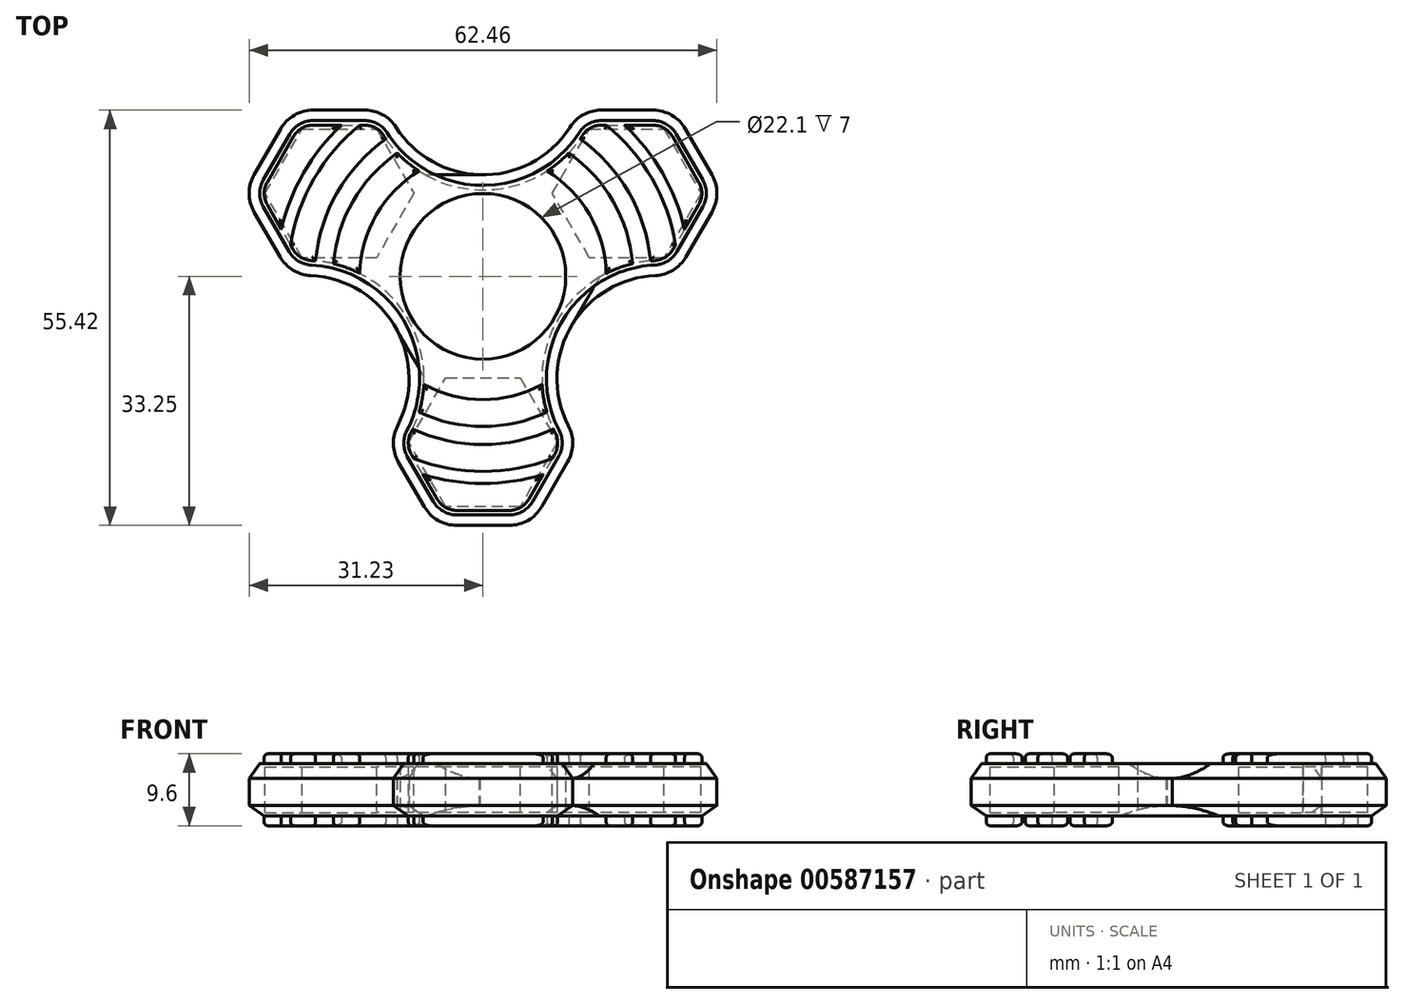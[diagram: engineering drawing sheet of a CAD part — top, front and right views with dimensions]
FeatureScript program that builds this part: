
annotation { "Feature Type Name" : "Feature", "Feature Type Description" : "" }
export const myFeature = defineFeature(function(context is Context, id is Id, definition is map)
    precondition{}
    {
        {
            var Q0;
            Q0=qCreatedBy(makeId("Top.planeOp"),FACE);
            var sketch = newSketch(context, id + "F0", { "sketchPlane" : qUnion([Q0])});
            skCircle(sketch, "E0", {"center": v(0, 0) * mm, "radius": 11.05 * mm});
            skCircle(sketch, "E1.cCircle", {"center": v(0, -22.15) * mm, "radius": 8.6 * mm, "construction": true});
            skLineSegment(sketch, "E1.0", {"start": v(4.97, -30.75) * mm, "end": v(-4.97, -30.75) * mm});
            skLineSegment(sketch, "E1.1", {"start": v(-4.97, -30.75) * mm, "end": v(-9.93, -22.15) * mm});
            skLineSegment(sketch, "E1.2", {"start": v(-9.93, -22.15) * mm, "end": v(-4.97, -13.55) * mm});
            skLineSegment(sketch, "E1.3", {"start": v(-4.97, -13.55) * mm, "end": v(4.97, -13.55) * mm});
            skLineSegment(sketch, "E1.4", {"start": v(4.97, -13.55) * mm, "end": v(9.93, -22.15) * mm});
            skLineSegment(sketch, "E1.5", {"start": v(9.93, -22.15) * mm, "end": v(4.97, -30.75) * mm});
            skPoint(sketch, "E1.0.midPoint", {"position": v(0, -30.75) * mm});
            skCircle(sketch, "E2.0", {"center": v(0, 0) * mm, "radius": 13.55 * mm});
            skLineSegment(sketch, "E3.3", {"start": v(3.52, -33.25) * mm, "end": v(-3.52, -33.25) * mm});
            skLineSegment(sketch, "E3.4", {"start": v(-7.85, -30.75) * mm, "end": v(-11.3, -24.77) * mm});
            skPoint(sketch, "E4.visualSharp", {"position": v(-6.4, -33.25) * mm});
            skArc(sketch, "E4.filletArc", {"start": v(-7.85, -30.75) * mm, "mid": v(-6.02, -32.58) * mm, "end": v(-3.52, -33.25) * mm});
            skPoint(sketch, "E5.visualSharp", {"position": v(6.4, -33.25) * mm});
            skArc(sketch, "E5.filletArc", {"start": v(3.52, -33.25) * mm, "mid": v(6.02, -32.58) * mm, "end": v(7.85, -30.75) * mm});
            skPoint(sketch, "E6.third.point", {"position": v(-11.94, -6.4) * mm});
            skPoint(sketch, "E7.third.point", {"position": v(11.98, -6.33) * mm});
            skLineSegment(sketch, "E8", {"start": v(11.3, -24.77) * mm, "end": v(7.85, -30.75) * mm});
            skArc(sketch, "E9", {"start": v(-11.42, -19.97) * mm, "mid": v(-9.89, -13.12) * mm, "end": v(-11.94, -6.4) * mm});
            skArc(sketch, "E10", {"start": v(11.98, -6.33) * mm, "mid": v(9.89, -13.08) * mm, "end": v(11.41, -19.97) * mm});
            skPoint(sketch, "E11.visualSharp", {"position": v(-12.82, -22.15) * mm});
            skArc(sketch, "E11.filletArc", {"start": v(-11.42, -19.97) * mm, "mid": v(-11.97, -22.38) * mm, "end": v(-11.3, -24.77) * mm});
            skPoint(sketch, "E12.visualSharp", {"position": v(12.82, -22.15) * mm});
            skArc(sketch, "E12.filletArc", {"start": v(11.3, -24.77) * mm, "mid": v(11.97, -22.38) * mm, "end": v(11.41, -19.97) * mm});
            skPoint(sketch, "E13.1.0", {"position": v(25.6, 22.17) * mm});
            skLineSegment(sketch, "E13.1.1", {"start": v(9.25, 11.07) * mm, "end": v(14.22, 19.68) * mm});
            skPoint(sketch, "E13.1.2", {"position": v(26.63, 15.37) * mm});
            skCircle(sketch, "E13.1.3", {"center": v(19.18, 11.07) * mm, "radius": 8.6 * mm, "construction": true});
            skLineSegment(sketch, "E13.1.4", {"start": v(29.11, 11.07) * mm, "end": v(24.15, 2.47) * mm});
            skLineSegment(sketch, "E13.1.5", {"start": v(15.8, 22.17) * mm, "end": v(22.7, 22.17) * mm});
            skPoint(sketch, "E13.1.6", {"position": v(32, 11.07) * mm});
            skPoint(sketch, "E13.1.7", {"position": v(25.6, -0.02) * mm});
            skLineSegment(sketch, "E13.1.8", {"start": v(27.03, 19.67) * mm, "end": v(30.56, 13.57) * mm});
            skLineSegment(sketch, "E13.1.9", {"start": v(24.15, 2.47) * mm, "end": v(14.22, 2.47) * mm});
            skLineSegment(sketch, "E13.1.10", {"start": v(14.22, 2.48) * mm, "end": v(9.25, 11.07) * mm});
            skLineSegment(sketch, "E13.1.11", {"start": v(24.15, 19.67) * mm, "end": v(29.11, 11.07) * mm});
            skLineSegment(sketch, "E13.1.12", {"start": v(14.22, 19.68) * mm, "end": v(24.15, 19.67) * mm});
            skPoint(sketch, "E13.1.13", {"position": v(12.77, 22.17) * mm});
            skLineSegment(sketch, "E13.1.14", {"start": v(30.56, 8.57) * mm, "end": v(27.1, 2.6) * mm});
            skArc(sketch, "E13.1.15", {"start": v(27.03, 19.67) * mm, "mid": v(25.2, 21.5) * mm, "end": v(22.7, 22.17) * mm});
            skArc(sketch, "E13.1.16", {"start": v(15.8, 22.17) * mm, "mid": v(13.4, 21.56) * mm, "end": v(11.59, 19.87) * mm});
            skArc(sketch, "E13.1.17", {"start": v(30.56, 8.57) * mm, "mid": v(31.23, 11.07) * mm, "end": v(30.56, 13.57) * mm});
            skArc(sketch, "E13.1.18", {"start": v(23, 0.1) * mm, "mid": v(25.37, 0.82) * mm, "end": v(27.1, 2.6) * mm});
            skArc(sketch, "E13.1.19", {"start": v(-0.5, 13.54) * mm, "mid": v(6.38, 15.1) * mm, "end": v(11.59, 19.87) * mm});
            skArc(sketch, "E13.1.20", {"start": v(23, 0.1) * mm, "mid": v(16.3, -2) * mm, "end": v(11.52, -7.14) * mm});
            skPoint(sketch, "E13.2.0", {"position": v(-32, 11.08) * mm});
            skLineSegment(sketch, "E13.2.1", {"start": v(-14.22, 2.48) * mm, "end": v(-24.15, 2.48) * mm});
            skPoint(sketch, "E13.2.2", {"position": v(-26.63, 15.38) * mm});
            skCircle(sketch, "E13.2.3", {"center": v(-19.18, 11.08) * mm, "radius": 8.6 * mm, "construction": true});
            skLineSegment(sketch, "E13.2.4", {"start": v(-24.15, 19.68) * mm, "end": v(-14.22, 19.68) * mm});
            skLineSegment(sketch, "E13.2.5", {"start": v(-27.1, 2.6) * mm, "end": v(-30.56, 8.58) * mm});
            skPoint(sketch, "E13.2.6", {"position": v(-25.6, 22.17) * mm});
            skPoint(sketch, "E13.2.7", {"position": v(-12.77, 22.17) * mm});
            skLineSegment(sketch, "E13.2.8", {"start": v(-30.56, 13.58) * mm, "end": v(-27.03, 19.67) * mm});
            skLineSegment(sketch, "E13.2.9", {"start": v(-14.22, 19.68) * mm, "end": v(-9.25, 11.08) * mm});
            skLineSegment(sketch, "E13.2.10", {"start": v(-9.25, 11.08) * mm, "end": v(-14.22, 2.48) * mm});
            skLineSegment(sketch, "E13.2.11", {"start": v(-29.11, 11.08) * mm, "end": v(-24.15, 19.68) * mm});
            skLineSegment(sketch, "E13.2.12", {"start": v(-24.15, 2.48) * mm, "end": v(-29.11, 11.08) * mm});
            skPoint(sketch, "E13.2.13", {"position": v(-25.6, -0.02) * mm});
            skLineSegment(sketch, "E13.2.14", {"start": v(-22.7, 22.17) * mm, "end": v(-15.8, 22.17) * mm});
            skArc(sketch, "E13.2.15", {"start": v(-30.56, 13.58) * mm, "mid": v(-31.23, 11.08) * mm, "end": v(-30.56, 8.58) * mm});
            skArc(sketch, "E13.2.16", {"start": v(-27.1, 2.6) * mm, "mid": v(-25.37, 0.82) * mm, "end": v(-23, 0.1) * mm});
            skArc(sketch, "E13.2.17", {"start": v(-22.7, 22.17) * mm, "mid": v(-25.2, 21.5) * mm, "end": v(-27.03, 19.67) * mm});
            skArc(sketch, "E13.2.18", {"start": v(-11.59, 19.87) * mm, "mid": v(-13.4, 21.56) * mm, "end": v(-15.8, 22.17) * mm});
            skArc(sketch, "E13.2.19", {"start": v(-11.47, -7.21) * mm, "mid": v(-16.27, -2.02) * mm, "end": v(-23, 0.1) * mm});
            skArc(sketch, "E13.2.20", {"start": v(-11.59, 19.87) * mm, "mid": v(-6.42, 15.13) * mm, "end": v(0.42, 13.54) * mm});
            skSolve(sketch);
        }
        {
            var Q0;
            Q0=qCreatedBy(makeId("Top.planeOp"),FACE);
            var sketch = newSketch(context, id + "F1", { "sketchPlane" : qUnion([Q0])});
            skArc(sketch, "E14.0", {"start": v(-9.64, -20.9) * mm, "mid": v(-7.9, -13.04) * mm, "end": v(-10.24, -5.36) * mm});
            skArc(sketch, "E14.1", {"start": v(-9.64, -20.9) * mm, "mid": v(-9.97, -22.34) * mm, "end": v(-9.57, -23.77) * mm});
            skLineSegment(sketch, "E14.2", {"start": v(-6.12, -29.75) * mm, "end": v(-9.57, -23.77) * mm});
            skArc(sketch, "E14.3", {"start": v(-6.12, -29.75) * mm, "mid": v(-5.02, -30.85) * mm, "end": v(-3.52, -31.25) * mm});
            skLineSegment(sketch, "E14.4", {"start": v(3.52, -31.25) * mm, "end": v(-3.52, -31.25) * mm});
            skArc(sketch, "E14.5", {"start": v(10.29, -5.27) * mm, "mid": v(7.89, -13) * mm, "end": v(9.64, -20.9) * mm});
            skArc(sketch, "E14.6", {"start": v(9.57, -23.77) * mm, "mid": v(9.97, -22.34) * mm, "end": v(9.64, -20.9) * mm});
            skLineSegment(sketch, "E14.7", {"start": v(9.57, -23.77) * mm, "end": v(6.12, -29.75) * mm});
            skArc(sketch, "E14.8", {"start": v(3.52, -31.25) * mm, "mid": v(5.02, -30.85) * mm, "end": v(6.12, -29.75) * mm});
            skLineSegment(sketch, "E15.1.0", {"start": v(28.82, 9.57) * mm, "end": v(25.37, 3.6) * mm});
            skArc(sketch, "E15.1.1", {"start": v(-0.58, 11.54) * mm, "mid": v(7.3, 13.33) * mm, "end": v(13.27, 18.8) * mm});
            skLineSegment(sketch, "E15.1.2", {"start": v(25.3, 18.67) * mm, "end": v(28.82, 12.58) * mm});
            skLineSegment(sketch, "E15.1.3", {"start": v(15.8, 20.17) * mm, "end": v(22.7, 20.17) * mm});
            skArc(sketch, "E15.1.4", {"start": v(22.91, 2.1) * mm, "mid": v(15.24, -0.31) * mm, "end": v(9.76, -6.19) * mm});
            skArc(sketch, "E15.1.5", {"start": v(22.91, 2.1) * mm, "mid": v(24.33, 2.53) * mm, "end": v(25.37, 3.6) * mm});
            skArc(sketch, "E15.1.6", {"start": v(28.82, 9.57) * mm, "mid": v(29.23, 11.07) * mm, "end": v(28.82, 12.58) * mm});
            skArc(sketch, "E15.1.7", {"start": v(15.8, 20.17) * mm, "mid": v(14.36, 19.8) * mm, "end": v(13.27, 18.8) * mm});
            skArc(sketch, "E15.1.8", {"start": v(25.3, 18.67) * mm, "mid": v(24.2, 19.77) * mm, "end": v(22.7, 20.17) * mm});
            skLineSegment(sketch, "E15.2.0", {"start": v(-22.7, 20.17) * mm, "end": v(-15.8, 20.17) * mm});
            skArc(sketch, "E15.2.1", {"start": v(-9.7, -6.27) * mm, "mid": v(-15.2, -0.33) * mm, "end": v(-22.91, 2.1) * mm});
            skLineSegment(sketch, "E15.2.2", {"start": v(-28.82, 12.58) * mm, "end": v(-25.3, 18.67) * mm});
            skLineSegment(sketch, "E15.2.3", {"start": v(-25.37, 3.6) * mm, "end": v(-28.82, 9.58) * mm});
            skArc(sketch, "E15.2.4", {"start": v(-13.27, 18.8) * mm, "mid": v(-7.35, 13.36) * mm, "end": v(0.48, 11.54) * mm});
            skArc(sketch, "E15.2.5", {"start": v(-13.27, 18.8) * mm, "mid": v(-14.36, 19.8) * mm, "end": v(-15.8, 20.17) * mm});
            skArc(sketch, "E15.2.6", {"start": v(-22.7, 20.17) * mm, "mid": v(-24.2, 19.77) * mm, "end": v(-25.3, 18.67) * mm});
            skArc(sketch, "E15.2.7", {"start": v(-25.37, 3.6) * mm, "mid": v(-24.33, 2.53) * mm, "end": v(-22.91, 2.1) * mm});
            skArc(sketch, "E15.2.8", {"start": v(-28.82, 12.58) * mm, "mid": v(-29.23, 11.08) * mm, "end": v(-28.82, 9.58) * mm});
            skPoint(sketch, "E15.center", {"position": v(0, 0) * mm});
            skCircle(sketch, "E16", {"center": v(0, 0) * mm, "radius": 27.65 * mm});
            skCircle(sketch, "E17", {"center": v(0, 0) * mm, "radius": 26.05 * mm});
            skCircle(sketch, "E18", {"center": v(0, 0) * mm, "radius": 22.45 * mm});
            skCircle(sketch, "E19", {"center": v(0, 0) * mm, "radius": 20.05 * mm});
            skCircle(sketch, "E20", {"center": v(0, 0) * mm, "radius": 16.45 * mm});
            skSolve(sketch);
        }
        {
            var Q0;
            {var subQ1=sQuery(id+"F0.wireOp",EDGE,"E13.2.1");Q0=makeQuery(id+"F0.imprint","IMPRINT",FACE,{"disambiguationData":[TD([[makeQuery(id+"F0.imprint","IMPRINT",EDGE,{"derivedFrom":subQ1}),1.0]])]});}
            var Q1;
            {var subQ1=sQuery(id+"F0.wireOp",EDGE,"E13.1.1");Q1=makeQuery(id+"F0.imprint","IMPRINT",FACE,{"disambiguationData":[TD([[makeQuery(id+"F0.imprint","IMPRINT",EDGE,{"derivedFrom":subQ1}),1.0]])]});}
            var Q2;
            Q2=makeQuery(id+"F0.imprint","IMPRINT",FACE,{"disambiguationData":[TD([[makeQuery(id+"F0.imprint","IMPRINT",EDGE,{"derivedFrom":sQuery(id+"F0.wireOp",EDGE,"E0")}),-1.0]])]});
            var Q3;
            Q3=makeQuery(id+"F0.imprint","IMPRINT",FACE,{"disambiguationData":[TD([[makeQuery(id+"F0.imprint","IMPRINT",EDGE,{"derivedFrom":sQuery(id+"F0.wireOp",EDGE,"E1.0")}),1.0]])]});
            var Q4;
            {var subQ3=sQuery(id+"F0.wireOp",EDGE,"E13.2.1");Q4=makeQuery(id+"F0.imprint","IMPRINT",FACE,{"disambiguationData":[TD([[makeQuery(id+"F0.imprint","IMPRINT",EDGE,{"derivedFrom":subQ3}),-1.0]])]});}
            var Q5;
            {var subQ3=sQuery(id+"F0.wireOp",EDGE,"E13.1.1");Q5=makeQuery(id+"F0.imprint","IMPRINT",FACE,{"disambiguationData":[TD([[makeQuery(id+"F0.imprint","IMPRINT",EDGE,{"derivedFrom":subQ3}),-1.0]])]});}
            var Q6;
            Q6=makeQuery(id+"F0.imprint","IMPRINT",FACE,{"disambiguationData":[TD([[makeQuery(id+"F0.imprint","IMPRINT",EDGE,{"derivedFrom":sQuery(id+"F0.wireOp",EDGE,"E1.0")}),-1.0]])]});
            var Q7;
            Q7=makeQuery(id+"F0.imprint","IMPRINT",FACE,{"disambiguationData":[TD([[makeQuery(id+"F0.imprint","IMPRINT",EDGE,{"derivedFrom":sQuery(id+"F0.wireOp",EDGE,"E0")}),1.0]])]});
            extrude(context, id + "F2", {"entities" : qUnion([Q0, Q1, Q2, Q3, Q4, Q5, Q6, Q7]), "endBound" : BoundingType.SYMMETRIC, "depth" : 7 * mm, "offsetDistance" : 25 * mm});
        }
        {
            var Q0;
            Q0=makeQuery(id+"F2.opExtrude","CAP_FACE",FACE,{"disambiguationData":[OSD([sQuery(id+"F0.wireOp",EDGE,"E0"),sQuery(id+"F0.wireOp",EDGE,"E2.0"),sQuery(id+"F0.wireOp",EDGE,"E3.3"),sQuery(id+"F0.wireOp",EDGE,"E3.4"),sQuery(id+"F0.wireOp",EDGE,"E4.filletArc"),sQuery(id+"F0.wireOp",EDGE,"E5.filletArc"),sQuery(id+"F0.wireOp",EDGE,"E8"),sQuery(id+"F0.wireOp",EDGE,"E9"),sQuery(id+"F0.wireOp",EDGE,"E10"),sQuery(id+"F0.wireOp",EDGE,"E11.filletArc"),sQuery(id+"F0.wireOp",EDGE,"E12.filletArc"),sQuery(id+"F0.wireOp",EDGE,"E13.1.5"),sQuery(id+"F0.wireOp",EDGE,"E13.1.8"),sQuery(id+"F0.wireOp",EDGE,"E13.1.14"),sQuery(id+"F0.wireOp",EDGE,"E13.1.15"),sQuery(id+"F0.wireOp",EDGE,"E13.1.16"),sQuery(id+"F0.wireOp",EDGE,"E13.1.17"),sQuery(id+"F0.wireOp",EDGE,"E13.1.18"),sQuery(id+"F0.wireOp",EDGE,"E13.1.19"),sQuery(id+"F0.wireOp",EDGE,"E13.1.20"),sQuery(id+"F0.wireOp",EDGE,"E13.2.5"),sQuery(id+"F0.wireOp",EDGE,"E13.2.8"),sQuery(id+"F0.wireOp",EDGE,"E13.2.14"),sQuery(id+"F0.wireOp",EDGE,"E13.2.15"),sQuery(id+"F0.wireOp",EDGE,"E13.2.16"),sQuery(id+"F0.wireOp",EDGE,"E13.2.17"),sQuery(id+"F0.wireOp",EDGE,"E13.2.18"),sQuery(id+"F0.wireOp",EDGE,"E13.2.19"),sQuery(id+"F0.wireOp",EDGE,"E13.2.20")])],"isStart":false});
            chamfer(context, id + "F3", {"entities" : qUnion([Q0]), "chamferType" : ChamferType.OFFSET_ANGLE, "width" : 2 * mm, "oppositeDirection" : false, "angle" : 35 * degree, "tangentPropagation" : true});
        }
        {
            var Q0;
            Q0=makeQuery(id+"F2.opExtrude","CAP_FACE",FACE,{"disambiguationData":[OSD([sQuery(id+"F0.wireOp",EDGE,"E2.0"),sQuery(id+"F0.wireOp",EDGE,"E3.3"),sQuery(id+"F0.wireOp",EDGE,"E3.4"),sQuery(id+"F0.wireOp",EDGE,"E4.filletArc"),sQuery(id+"F0.wireOp",EDGE,"E5.filletArc"),sQuery(id+"F0.wireOp",EDGE,"E8"),sQuery(id+"F0.wireOp",EDGE,"E9"),sQuery(id+"F0.wireOp",EDGE,"E10"),sQuery(id+"F0.wireOp",EDGE,"E11.filletArc"),sQuery(id+"F0.wireOp",EDGE,"E12.filletArc"),sQuery(id+"F0.wireOp",EDGE,"E13.1.5"),sQuery(id+"F0.wireOp",EDGE,"E13.1.8"),sQuery(id+"F0.wireOp",EDGE,"E13.1.14"),sQuery(id+"F0.wireOp",EDGE,"E13.1.15"),sQuery(id+"F0.wireOp",EDGE,"E13.1.16"),sQuery(id+"F0.wireOp",EDGE,"E13.1.17"),sQuery(id+"F0.wireOp",EDGE,"E13.1.18"),sQuery(id+"F0.wireOp",EDGE,"E13.1.19"),sQuery(id+"F0.wireOp",EDGE,"E13.1.20"),sQuery(id+"F0.wireOp",EDGE,"E13.2.5"),sQuery(id+"F0.wireOp",EDGE,"E13.2.8"),sQuery(id+"F0.wireOp",EDGE,"E13.2.14"),sQuery(id+"F0.wireOp",EDGE,"E13.2.15"),sQuery(id+"F0.wireOp",EDGE,"E13.2.16"),sQuery(id+"F0.wireOp",EDGE,"E13.2.17"),sQuery(id+"F0.wireOp",EDGE,"E13.2.18"),sQuery(id+"F0.wireOp",EDGE,"E13.2.19"),sQuery(id+"F0.wireOp",EDGE,"E13.2.20")])],"isStart":true});
            chamfer(context, id + "F4", {"entities" : qUnion([Q0]), "chamferType" : ChamferType.OFFSET_ANGLE, "width" : 2 * mm, "oppositeDirection" : false, "angle" : 35 * degree, "tangentPropagation" : true});
        }
        {
            var Q0;
            Q0=makeQuery(id+"F1.imprint","IMPRINT",FACE,{"disambiguationData":[TD([[makeQuery(id+"F1.imprint","IMPRINT",EDGE,{"derivedFrom":sQuery(id+"F1.wireOp",EDGE,"E15.2.2")}),-1.0]])]});
            var Q1;
            {var subQ0=sQuery(id+"F1.wireOp",EDGE,"E15.2.5");Q1=makeQuery(id+"F1.imprint","IMPRINT",FACE,{"disambiguationData":[TD([[makeQuery(id+"F1.imprint","IMPRINT",EDGE,{"derivedFrom":subQ0}),1.0]])]});}
            var Q2;
            {var subQ0=sQuery(id+"F1.wireOp",EDGE,"E20");var subQ1=sQuery(id+"F1.wireOp",EDGE,"E15.2.1");var subQ2=makeQuery(id+"F1.imprint","INTERSECT",VERTEX,{"derivedFrom":[subQ1,subQ0]});Q2=makeQuery(id+"F1.imprint","IMPRINT",FACE,{"disambiguationData":[TD([[makeQuery(id+"F1.imprint","IMPRINT",EDGE,{"disambiguationData":[TD([[subQ2,-1.0]])],"derivedFrom":subQ1}),-1.0]])]});}
            var Q3;
            {var subQ0=sQuery(id+"F1.wireOp",EDGE,"E20");var subQ1=sQuery(id+"F1.wireOp",EDGE,"E15.1.1");var subQ2=makeQuery(id+"F1.imprint","INTERSECT",VERTEX,{"derivedFrom":[subQ1,subQ0]});Q3=makeQuery(id+"F1.imprint","IMPRINT",FACE,{"disambiguationData":[TD([[makeQuery(id+"F1.imprint","IMPRINT",EDGE,{"disambiguationData":[TD([[subQ2,-1.0]])],"derivedFrom":subQ1}),-1.0]])]});}
            var Q4;
            {var subQ0=sQuery(id+"F1.wireOp",EDGE,"E15.1.5");Q4=makeQuery(id+"F1.imprint","IMPRINT",FACE,{"disambiguationData":[TD([[makeQuery(id+"F1.imprint","IMPRINT",EDGE,{"derivedFrom":subQ0}),1.0]])]});}
            var Q5;
            Q5=makeQuery(id+"F1.imprint","IMPRINT",FACE,{"disambiguationData":[TD([[makeQuery(id+"F1.imprint","IMPRINT",EDGE,{"derivedFrom":sQuery(id+"F1.wireOp",EDGE,"E15.1.2")}),-1.0]])]});
            var Q6;
            {var subQ4=sQuery(id+"F1.wireOp",EDGE,"E14.3");Q6=makeQuery(id+"F1.imprint","IMPRINT",FACE,{"disambiguationData":[TD([[makeQuery(id+"F1.imprint","IMPRINT",EDGE,{"derivedFrom":subQ4}),1.0]])]});}
            var Q7;
            {var subQ4=sQuery(id+"F1.wireOp",EDGE,"E14.1");Q7=makeQuery(id+"F1.imprint","IMPRINT",FACE,{"disambiguationData":[TD([[makeQuery(id+"F1.imprint","IMPRINT",EDGE,{"derivedFrom":subQ4}),1.0]])]});}
            var Q8;
            {var subQ0=sQuery(id+"F1.wireOp",EDGE,"E20");var subQ1=sQuery(id+"F1.wireOp",EDGE,"E14.0");var subQ2=makeQuery(id+"F1.imprint","INTERSECT",VERTEX,{"derivedFrom":[subQ1,subQ0]});Q8=makeQuery(id+"F1.imprint","IMPRINT",FACE,{"disambiguationData":[TD([[makeQuery(id+"F1.imprint","IMPRINT",EDGE,{"disambiguationData":[TD([[subQ2,1.0]])],"derivedFrom":subQ1}),-1.0]])]});}
            extrude(context, id + "F5", {"entities" : qUnion([Q0, Q1, Q2, Q3, Q4, Q5, Q6, Q7, Q8]), "operationType" : NewBodyOperationType.ADD, "endBound" : BoundingType.SYMMETRIC, "depth" : 9.6 * mm, "offsetDistance" : 25 * mm});
        }
        {
            var Q0;
            Q0=makeQuery(id+"F5.opExtrude","CAP_FACE",FACE,{"disambiguationData":[OSD([sQuery(id+"F1.wireOp",EDGE,"E14.2"),sQuery(id+"F1.wireOp",EDGE,"E14.3"),sQuery(id+"F1.wireOp",EDGE,"E14.4"),sQuery(id+"F1.wireOp",EDGE,"E14.7"),sQuery(id+"F1.wireOp",EDGE,"E14.8"),sQuery(id+"F1.wireOp",EDGE,"E16")])],"isStart":false});
            var Q1;
            Q1=makeQuery(id+"F5.opExtrude","CAP_FACE",FACE,{"disambiguationData":[OSD([sQuery(id+"F1.wireOp",EDGE,"E14.0"),sQuery(id+"F1.wireOp",EDGE,"E14.1"),sQuery(id+"F1.wireOp",EDGE,"E14.2"),sQuery(id+"F1.wireOp",EDGE,"E14.5"),sQuery(id+"F1.wireOp",EDGE,"E14.6"),sQuery(id+"F1.wireOp",EDGE,"E14.7"),sQuery(id+"F1.wireOp",EDGE,"E17"),sQuery(id+"F1.wireOp",EDGE,"E18")])],"isStart":false});
            var Q2;
            Q2=makeQuery(id+"F5.opExtrude","CAP_FACE",FACE,{"disambiguationData":[OSD([sQuery(id+"F1.wireOp",EDGE,"E14.0"),sQuery(id+"F1.wireOp",EDGE,"E14.5"),sQuery(id+"F1.wireOp",EDGE,"E19"),sQuery(id+"F1.wireOp",EDGE,"E20")])],"isStart":false});
            var Q3;
            Q3=makeQuery(id+"F5.opExtrude","CAP_FACE",FACE,{"disambiguationData":[OSD([sQuery(id+"F1.wireOp",EDGE,"E15.1.1"),sQuery(id+"F1.wireOp",EDGE,"E15.1.4"),sQuery(id+"F1.wireOp",EDGE,"E19"),sQuery(id+"F1.wireOp",EDGE,"E20")])],"isStart":false});
            var Q4;
            Q4=makeQuery(id+"F5.opExtrude","CAP_FACE",FACE,{"disambiguationData":[OSD([sQuery(id+"F1.wireOp",EDGE,"E15.1.0"),sQuery(id+"F1.wireOp",EDGE,"E15.1.1"),sQuery(id+"F1.wireOp",EDGE,"E15.1.3"),sQuery(id+"F1.wireOp",EDGE,"E15.1.4"),sQuery(id+"F1.wireOp",EDGE,"E15.1.5"),sQuery(id+"F1.wireOp",EDGE,"E15.1.7"),sQuery(id+"F1.wireOp",EDGE,"E17"),sQuery(id+"F1.wireOp",EDGE,"E18")])],"isStart":false});
            var Q5;
            Q5=makeQuery(id+"F5.opExtrude","CAP_FACE",FACE,{"disambiguationData":[OSD([sQuery(id+"F1.wireOp",EDGE,"E15.1.0"),sQuery(id+"F1.wireOp",EDGE,"E15.1.2"),sQuery(id+"F1.wireOp",EDGE,"E15.1.3"),sQuery(id+"F1.wireOp",EDGE,"E15.1.6"),sQuery(id+"F1.wireOp",EDGE,"E15.1.8"),sQuery(id+"F1.wireOp",EDGE,"E16")])],"isStart":false});
            var Q6;
            Q6=makeQuery(id+"F5.opExtrude","CAP_FACE",FACE,{"disambiguationData":[OSD([sQuery(id+"F1.wireOp",EDGE,"E15.2.1"),sQuery(id+"F1.wireOp",EDGE,"E15.2.4"),sQuery(id+"F1.wireOp",EDGE,"E19"),sQuery(id+"F1.wireOp",EDGE,"E20")])],"isStart":false});
            var Q7;
            Q7=makeQuery(id+"F5.opExtrude","CAP_FACE",FACE,{"disambiguationData":[OSD([sQuery(id+"F1.wireOp",EDGE,"E15.2.0"),sQuery(id+"F1.wireOp",EDGE,"E15.2.1"),sQuery(id+"F1.wireOp",EDGE,"E15.2.3"),sQuery(id+"F1.wireOp",EDGE,"E15.2.4"),sQuery(id+"F1.wireOp",EDGE,"E15.2.5"),sQuery(id+"F1.wireOp",EDGE,"E15.2.7"),sQuery(id+"F1.wireOp",EDGE,"E17"),sQuery(id+"F1.wireOp",EDGE,"E18")])],"isStart":false});
            var Q8;
            Q8=makeQuery(id+"F5.opExtrude","CAP_FACE",FACE,{"disambiguationData":[OSD([sQuery(id+"F1.wireOp",EDGE,"E15.2.0"),sQuery(id+"F1.wireOp",EDGE,"E15.2.2"),sQuery(id+"F1.wireOp",EDGE,"E15.2.3"),sQuery(id+"F1.wireOp",EDGE,"E15.2.6"),sQuery(id+"F1.wireOp",EDGE,"E15.2.8"),sQuery(id+"F1.wireOp",EDGE,"E16")])],"isStart":false});
            var Q9;
            Q9=makeQuery(id+"F5.opExtrude","CAP_FACE",FACE,{"disambiguationData":[OSD([sQuery(id+"F1.wireOp",EDGE,"E15.1.0"),sQuery(id+"F1.wireOp",EDGE,"E15.1.2"),sQuery(id+"F1.wireOp",EDGE,"E15.1.3"),sQuery(id+"F1.wireOp",EDGE,"E15.1.6"),sQuery(id+"F1.wireOp",EDGE,"E15.1.8"),sQuery(id+"F1.wireOp",EDGE,"E16")])],"isStart":true});
            var Q10;
            Q10=makeQuery(id+"F5.opExtrude","CAP_FACE",FACE,{"disambiguationData":[OSD([sQuery(id+"F1.wireOp",EDGE,"E15.1.0"),sQuery(id+"F1.wireOp",EDGE,"E15.1.1"),sQuery(id+"F1.wireOp",EDGE,"E15.1.3"),sQuery(id+"F1.wireOp",EDGE,"E15.1.4"),sQuery(id+"F1.wireOp",EDGE,"E15.1.5"),sQuery(id+"F1.wireOp",EDGE,"E15.1.7"),sQuery(id+"F1.wireOp",EDGE,"E17"),sQuery(id+"F1.wireOp",EDGE,"E18")])],"isStart":true});
            var Q11;
            Q11=makeQuery(id+"F5.opExtrude","CAP_FACE",FACE,{"disambiguationData":[OSD([sQuery(id+"F1.wireOp",EDGE,"E15.1.1"),sQuery(id+"F1.wireOp",EDGE,"E15.1.4"),sQuery(id+"F1.wireOp",EDGE,"E19"),sQuery(id+"F1.wireOp",EDGE,"E20")])],"isStart":true});
            var Q12;
            Q12=makeQuery(id+"F5.opExtrude","CAP_FACE",FACE,{"disambiguationData":[OSD([sQuery(id+"F1.wireOp",EDGE,"E14.0"),sQuery(id+"F1.wireOp",EDGE,"E14.5"),sQuery(id+"F1.wireOp",EDGE,"E19"),sQuery(id+"F1.wireOp",EDGE,"E20")])],"isStart":true});
            var Q13;
            Q13=makeQuery(id+"F5.opExtrude","CAP_FACE",FACE,{"disambiguationData":[OSD([sQuery(id+"F1.wireOp",EDGE,"E14.0"),sQuery(id+"F1.wireOp",EDGE,"E14.1"),sQuery(id+"F1.wireOp",EDGE,"E14.2"),sQuery(id+"F1.wireOp",EDGE,"E14.5"),sQuery(id+"F1.wireOp",EDGE,"E14.6"),sQuery(id+"F1.wireOp",EDGE,"E14.7"),sQuery(id+"F1.wireOp",EDGE,"E17"),sQuery(id+"F1.wireOp",EDGE,"E18")])],"isStart":true});
            var Q14;
            Q14=makeQuery(id+"F5.opExtrude","CAP_FACE",FACE,{"disambiguationData":[OSD([sQuery(id+"F1.wireOp",EDGE,"E14.2"),sQuery(id+"F1.wireOp",EDGE,"E14.3"),sQuery(id+"F1.wireOp",EDGE,"E14.4"),sQuery(id+"F1.wireOp",EDGE,"E14.7"),sQuery(id+"F1.wireOp",EDGE,"E14.8"),sQuery(id+"F1.wireOp",EDGE,"E16")])],"isStart":true});
            var Q15;
            Q15=makeQuery(id+"F5.opExtrude","CAP_FACE",FACE,{"disambiguationData":[OSD([sQuery(id+"F1.wireOp",EDGE,"E15.2.1"),sQuery(id+"F1.wireOp",EDGE,"E15.2.4"),sQuery(id+"F1.wireOp",EDGE,"E19"),sQuery(id+"F1.wireOp",EDGE,"E20")])],"isStart":true});
            var Q16;
            Q16=makeQuery(id+"F5.opExtrude","CAP_FACE",FACE,{"disambiguationData":[OSD([sQuery(id+"F1.wireOp",EDGE,"E15.2.0"),sQuery(id+"F1.wireOp",EDGE,"E15.2.1"),sQuery(id+"F1.wireOp",EDGE,"E15.2.3"),sQuery(id+"F1.wireOp",EDGE,"E15.2.4"),sQuery(id+"F1.wireOp",EDGE,"E15.2.5"),sQuery(id+"F1.wireOp",EDGE,"E15.2.7"),sQuery(id+"F1.wireOp",EDGE,"E17"),sQuery(id+"F1.wireOp",EDGE,"E18")])],"isStart":true});
            var Q17;
            Q17=makeQuery(id+"F5.opExtrude","CAP_FACE",FACE,{"disambiguationData":[OSD([sQuery(id+"F1.wireOp",EDGE,"E15.2.0"),sQuery(id+"F1.wireOp",EDGE,"E15.2.2"),sQuery(id+"F1.wireOp",EDGE,"E15.2.3"),sQuery(id+"F1.wireOp",EDGE,"E15.2.6"),sQuery(id+"F1.wireOp",EDGE,"E15.2.8"),sQuery(id+"F1.wireOp",EDGE,"E16")])],"isStart":true});
            fillet(context, id + "F6", {"entities" : qUnion([Q0, Q1, Q2, Q3, Q4, Q5, Q6, Q7, Q8, Q9, Q10, Q11, Q12, Q13, Q14, Q15, Q16, Q17]), "radius" : 0.5 * mm, "allowEdgeOverflow" : false});
        }
        {
            var Q0;
            {var subQ3=sQuery(id+"F0.wireOp",EDGE,"E13.2.1");Q0=makeQuery(id+"F0.imprint","IMPRINT",FACE,{"disambiguationData":[TD([[makeQuery(id+"F0.imprint","IMPRINT",EDGE,{"derivedFrom":subQ3}),-1.0]])]});}
            var Q1;
            {var subQ3=sQuery(id+"F0.wireOp",EDGE,"E13.1.1");Q1=makeQuery(id+"F0.imprint","IMPRINT",FACE,{"disambiguationData":[TD([[makeQuery(id+"F0.imprint","IMPRINT",EDGE,{"derivedFrom":subQ3}),-1.0]])]});}
            var Q2;
            Q2=makeQuery(id+"F0.imprint","IMPRINT",FACE,{"disambiguationData":[TD([[makeQuery(id+"F0.imprint","IMPRINT",EDGE,{"derivedFrom":sQuery(id+"F0.wireOp",EDGE,"E1.0")}),-1.0]])]});
            extrude(context, id + "F7", {"entities" : qUnion([Q0, Q1, Q2]), "operationType" : NewBodyOperationType.REMOVE, "endBound" : BoundingType.SYMMETRIC, "oppositeDirection" : true, "depth" : 6.1 * mm, "offsetDistance" : 25 * mm});
        }
        {
            var Q0;
            Q0=makeQuery(id+"F0.imprint","IMPRINT",FACE,{"disambiguationData":[TD([[makeQuery(id+"F0.imprint","IMPRINT",EDGE,{"derivedFrom":sQuery(id+"F0.wireOp",EDGE,"E0")}),1.0]])]});
            extrude(context, id + "F8", {"entities" : qUnion([Q0]), "operationType" : NewBodyOperationType.REMOVE, "endBound" : BoundingType.SYMMETRIC, "depth" : 25 * mm, "offsetDistance" : 25 * mm});
        }
    });
